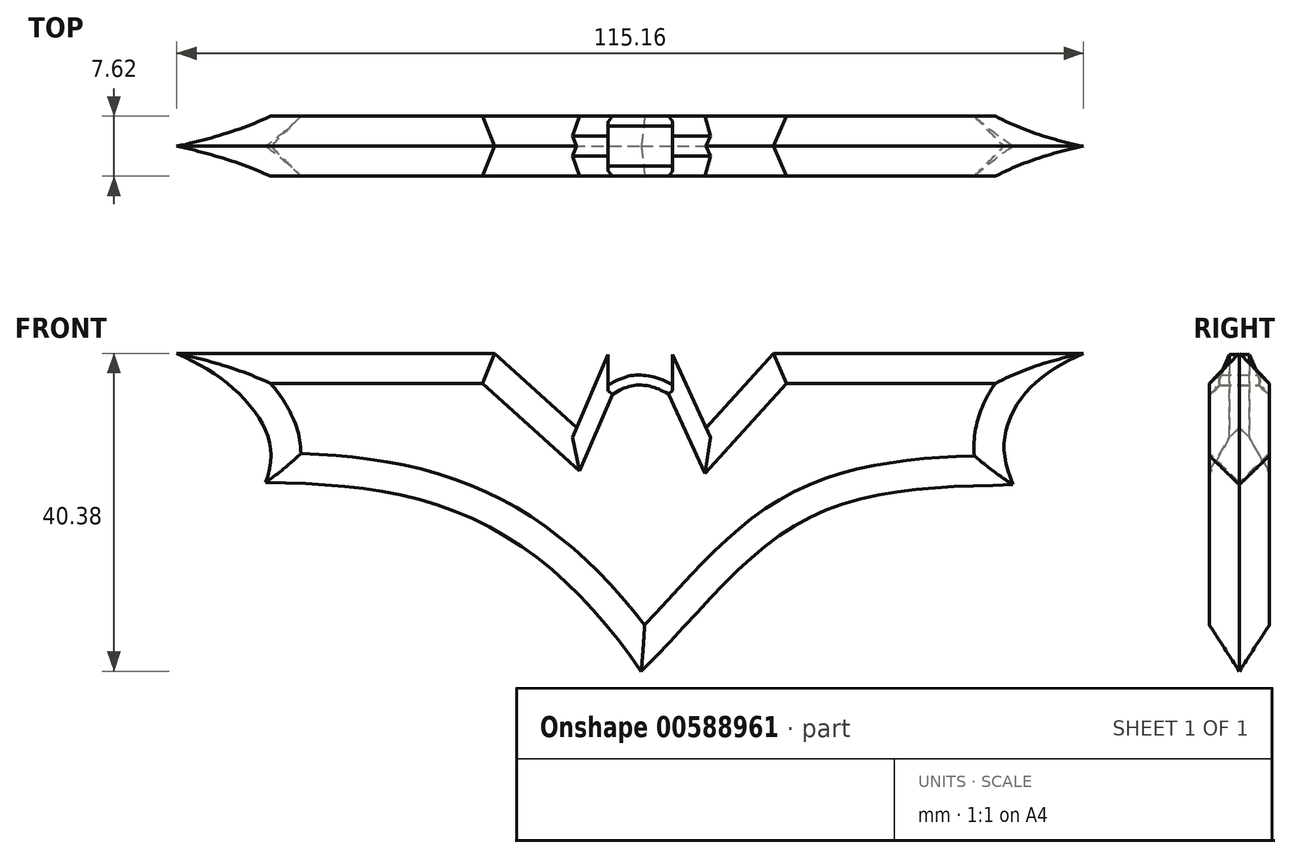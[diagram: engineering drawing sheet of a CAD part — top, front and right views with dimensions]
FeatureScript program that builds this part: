
annotation { "Feature Type Name" : "Feature", "Feature Type Description" : "" }
export const myFeature = defineFeature(function(context is Context, id is Id, definition is map)
    precondition{}
    {
        {
            var Q0;
            Q0=qCreatedBy(makeId("Front.planeOp"),FACE);
            var sketch = newSketch(context, id + "F0", { "sketchPlane" : qUnion([Q0])});
            skFitSpline(sketch, "E0", {"points": [v(-4.04, 7.82) * mm, v(0, 9.15) * mm, v(4.18, 7.92) * mm], "startDerivative": vector(10.5, 6.5) * mm, "endDerivative": vector(9.66, -5.41) * mm});
            skLineSegment(sketch, "E1", {"start": v(4.18, 7.92) * mm, "end": v(4.18, 11.77) * mm});
            skLineSegment(sketch, "E2", {"start": v(-4.04, 7.82) * mm, "end": v(-4.04, 11.77) * mm});
            skLineSegment(sketch, "E3", {"start": v(-4.04, 11.77) * mm, "end": v(-7.48, 3.7) * mm});
            skLineSegment(sketch, "E4", {"start": v(-7.48, 3.7) * mm, "end": v(-17.97, 13.18) * mm});
            skLineSegment(sketch, "E5", {"start": v(-17.97, 13.18) * mm, "end": v(-66.3, 13.18) * mm});
            skLineSegment(sketch, "E6", {"start": v(4.18, 11.77) * mm, "end": v(7.87, 3.7) * mm});
            skLineSegment(sketch, "E7", {"start": v(7.87, 3.7) * mm, "end": v(16.43, 13.18) * mm});
            skLineSegment(sketch, "E8", {"start": v(16.43, 13.18) * mm, "end": v(64.76, 13.18) * mm});
            skPoint(sketch, "E8.endSnap0", {"position": v(-42.13, 13.18) * mm});
            skFitSpline(sketch, "E9", {"points": [v(-66.3, 13.18) * mm, v(-49.5, 3.16) * mm, v(-49.44, -5.73) * mm], "startDerivative": vector(48.97, -13.29) * mm, "endDerivative": vector(-15.26, -30.52) * mm});
            skFitSpline(sketch, "E10", {"points": [v(-49.44, -5.73) * mm, v(-22.51, -9.89) * mm, v(0, -30.44) * mm], "startDerivative": vector(60.8, -0.3) * mm, "endDerivative": vector(38.82, -58.55) * mm});
            skFitSpline(sketch, "E11", {"points": [v(64.76, 13.18) * mm, v(48.12, 2.9) * mm, v(49.44, -5.98) * mm], "startDerivative": vector(-55.92, -12.26) * mm, "endDerivative": vector(15.36, -29.62) * mm});
            skFitSpline(sketch, "E12", {"points": [v(49.44, -5.98) * mm, v(22.51, -9.89) * mm, v(0, -30.44) * mm], "startDerivative": vector(-52.37, -1.8) * mm, "endDerivative": vector(-48.4, -45.88) * mm});
            skSolve(sketch);
        }
        {
            var Q0;
            Q0=makeQuery(id+"F0.imprint","IMPRINT",FACE,{"disambiguationData":[TD([[makeQuery(id+"F0.imprint","IMPRINT",EDGE,{"derivedFrom":sQuery(id+"F0.wireOp",EDGE,"E0")}),-1.0]])]});
            extrude(context, id + "F1", {"entities" : qUnion([Q0]), "depth" : 3.8 * mm, "offsetDistance" : 25.4 * mm});
        }
        {
            var Q0;
            Q0=makeQuery(id+"F1.opExtrude","CAP_EDGE",EDGE,{"disambiguationData":[OSD([sQuery(id+"F0.wireOp",EDGE,"E5")])],"isStart":false});
            var Q1;
            Q1=makeQuery(id+"F1.opExtrude","CAP_EDGE",EDGE,{"disambiguationData":[OSD([sQuery(id+"F0.wireOp",EDGE,"E8")])],"isStart":false});
            var Q2;
            Q2=makeQuery(id+"F1.opExtrude","CAP_EDGE",EDGE,{"disambiguationData":[OSD([sQuery(id+"F0.wireOp",EDGE,"E4")])],"isStart":false});
            var Q3;
            Q3=makeQuery(id+"F1.opExtrude","CAP_EDGE",EDGE,{"disambiguationData":[OSD([sQuery(id+"F0.wireOp",EDGE,"E7")])],"isStart":false});
            var Q4;
            Q4=makeQuery(id+"F1.opExtrude","CAP_EDGE",EDGE,{"disambiguationData":[OSD([sQuery(id+"F0.wireOp",EDGE,"E11")])],"isStart":false});
            var Q5;
            Q5=makeQuery(id+"F1.opExtrude","CAP_EDGE",EDGE,{"disambiguationData":[OSD([sQuery(id+"F0.wireOp",EDGE,"E9")])],"isStart":false});
            var Q6;
            Q6=makeQuery(id+"F1.opExtrude","CAP_EDGE",EDGE,{"disambiguationData":[OSD([sQuery(id+"F0.wireOp",EDGE,"E10")])],"isStart":false});
            var Q7;
            Q7=makeQuery(id+"F1.opExtrude","CAP_EDGE",EDGE,{"disambiguationData":[OSD([sQuery(id+"F0.wireOp",EDGE,"E12")])],"isStart":false});
            chamfer(context, id + "F2", {"entities" : qUnion([Q0, Q1, Q2, Q3, Q4, Q5, Q6, Q7]), "chamferType" : ChamferType.OFFSET_ANGLE, "width" : 5.08 * mm, "oppositeDirection" : false, "angle" : 45 * degree, "tangentPropagation" : true});
        }
        {
            var Q0;
            Q0=makeQuery(id+"F1.opExtrude","CAP_EDGE",EDGE,{"disambiguationData":[OSD([sQuery(id+"F0.wireOp",EDGE,"E3")])],"isStart":false});
            var Q1;
            Q1=makeQuery(id+"F1.opExtrude","CAP_EDGE",EDGE,{"disambiguationData":[OSD([sQuery(id+"F0.wireOp",EDGE,"E6")])],"isStart":false});
            chamfer(context, id + "F3", {"entities" : qUnion([Q0, Q1]), "chamferType" : ChamferType.OFFSET_ANGLE, "width" : 2.54 * mm, "oppositeDirection" : false, "angle" : 45 * degree, "tangentPropagation" : true});
        }
        {
            var Q0;
            Q0=makeQuery(id+"F1.opExtrude","CAP_EDGE",EDGE,{"disambiguationData":[OSD([sQuery(id+"F0.wireOp",EDGE,"E0")])],"isStart":false});
            chamfer(context, id + "F4", {"entities" : qUnion([Q0]), "width" : 1.27 * mm, "tangentPropagation" : true});
        }
        {
            var Q0;
            Q0=makeQuery(id+"F1.opExtrude","SWEPT_BODY",BODY,{"disambiguationData":[OSD([sQuery(id+"F0.wireOp",EDGE,"E0"),sQuery(id+"F0.wireOp",EDGE,"E1"),sQuery(id+"F0.wireOp",EDGE,"E2"),sQuery(id+"F0.wireOp",EDGE,"E3"),sQuery(id+"F0.wireOp",EDGE,"E4"),sQuery(id+"F0.wireOp",EDGE,"E5"),sQuery(id+"F0.wireOp",EDGE,"E6"),sQuery(id+"F0.wireOp",EDGE,"E7"),sQuery(id+"F0.wireOp",EDGE,"E8"),sQuery(id+"F0.wireOp",EDGE,"E9"),sQuery(id+"F0.wireOp",EDGE,"E10"),sQuery(id+"F0.wireOp",EDGE,"E11"),sQuery(id+"F0.wireOp",EDGE,"E12")])]});
            var Q1;
            Q1=qCreatedBy(makeId("Front.planeOp"),FACE);
            mirror(context, id + "F5", {"operationType" : NewBodyOperationType.ADD, "entities" : qUnion([Q0]), "mirrorPlane" : qUnion([Q1])});
        }
    });
